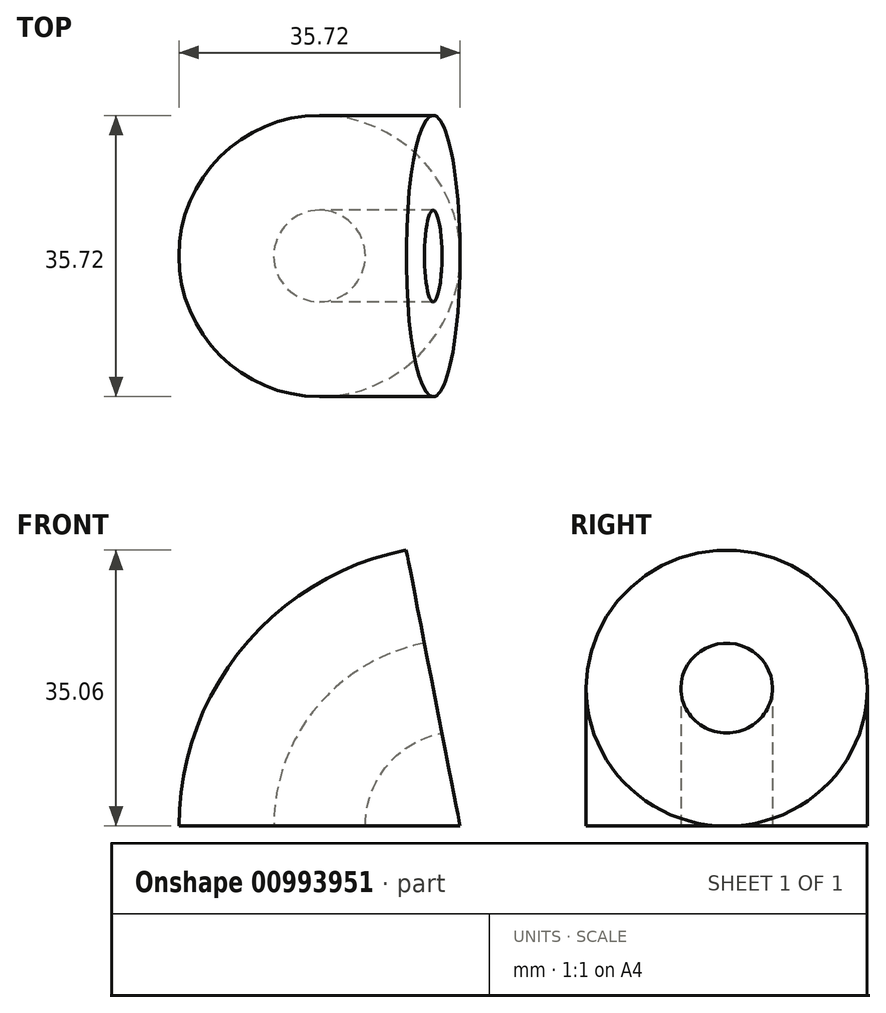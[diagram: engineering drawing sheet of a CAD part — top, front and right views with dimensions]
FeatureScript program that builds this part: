
annotation { "Feature Type Name" : "Feature", "Feature Type Description" : "" }
export const myFeature = defineFeature(function(context is Context, id is Id, definition is map)
    precondition{}
    {
        {
            var Q0;
            Q0=qCreatedBy(makeId("Top.planeOp"),FACE);
            var sketch = newSketch(context, id + "F0", { "sketchPlane" : qUnion([Q0])});
            skLineSegment(sketch, "E0", {"start": v(0, 34.93) * mm, "end": v(0, -36.06) * mm, "construction": true});
            skLineSegment(sketch, "E1", {"start": v(-40.4, 0) * mm, "end": v(30.4, 0) * mm, "construction": true});
            skSolve(sketch);
        }
        {
            var Q0;
            Q0=qCreatedBy(makeId("Top.planeOp"),FACE);
            var sketch = newSketch(context, id + "F1", { "sketchPlane" : qUnion([Q0])});
            skCircle(sketch, "E2", {"center": v(0, 0) * mm, "radius": 17.86 * mm});
            skPoint(sketch, "E3", {"position": v(17.86, 0) * mm});
            skSolve(sketch);
        }
        {
            var Q0;
            Q0=qCreatedBy(makeId("Front.planeOp"),FACE);
            var sketch = newSketch(context, id + "F2", { "sketchPlane" : qUnion([Q0])});
            skArc(sketch, "E4", {"start": v(0, 0) * mm, "mid": v(4.07, 11.35) * mm, "end": v(14.44, 17.53) * mm});
            skSolve(sketch);
        }
        {
            var Q0;
            Q0=makeQuery(id+"F1.imprint","IMPRINT",FACE,{"disambiguationData":[TD([[makeQuery(id+"F1.imprint","IMPRINT",EDGE,{"derivedFrom":sQuery(id+"F1.wireOp",EDGE,"E2")}),1.0]])]});
            var Q1;
            Q1=sQuery(id+"F2.wireOp",EDGE,"E4");
            sweep(context, id + "F3", {"profiles" : qUnion([Q0]), "path" : qUnion([Q1])});
        }
        {
            var Q0;
            Q0=qCreatedBy(makeId("Top.planeOp"),FACE);
            var sketch = newSketch(context, id + "F4", { "sketchPlane" : qUnion([Q0])});
            skCircle(sketch, "E5", {"center": v(0, 0) * mm, "radius": 5.82 * mm});
            skSolve(sketch);
        }
        {
            var Q0;
            Q0=makeQuery(id+"F4.imprint","IMPRINT",FACE,{"disambiguationData":[TD([[makeQuery(id+"F4.imprint","IMPRINT",EDGE,{"derivedFrom":sQuery(id+"F4.wireOp",EDGE,"E5")}),1.0]])]});
            var Q1;
            Q1=sQuery(id+"F2.wireOp",EDGE,"E4");
            sweep(context, id + "F5", {"operationType" : NewBodyOperationType.REMOVE, "profiles" : qUnion([Q0]), "path" : qUnion([Q1])});
        }
    });
